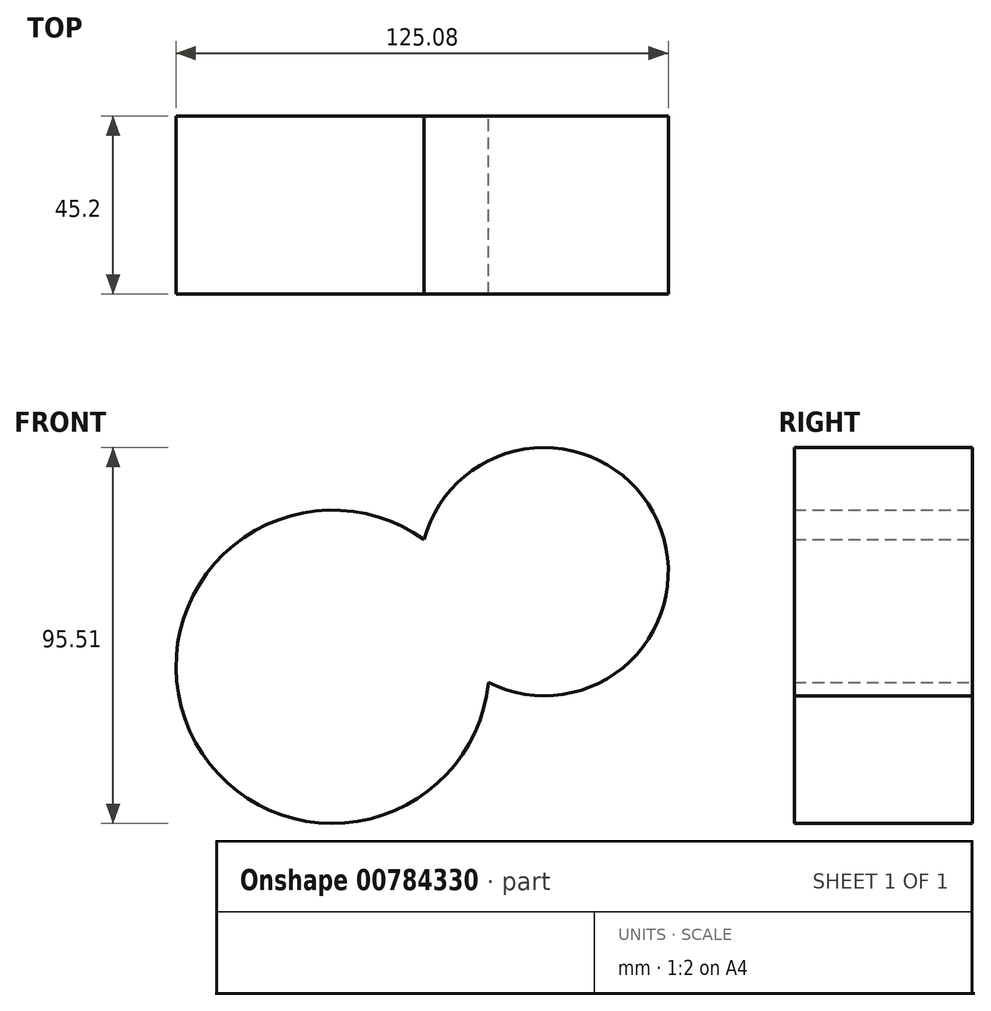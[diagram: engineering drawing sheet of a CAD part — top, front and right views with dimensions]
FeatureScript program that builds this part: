
annotation { "Feature Type Name" : "Feature", "Feature Type Description" : "" }
export const myFeature = defineFeature(function(context is Context, id is Id, definition is map)
    precondition{}
    {
        {
            var Q0;
            Q0=qCreatedBy(makeId("Front.planeOp"),FACE);
            var sketch = newSketch(context, id + "F0", { "sketchPlane" : qUnion([Q0])});
            skCircle(sketch, "E0", {"center": v(-22.89, 16.63) * mm, "radius": 39.8 * mm});
            skCircle(sketch, "E1", {"center": v(30.85, 40.8) * mm, "radius": 31.54 * mm});
            skSolve(sketch);
        }
        {
            var Q0;
            Q0 = qSketchRegion(id + "F0", true);
            extrude(context, id + "F1", {"entities" : qUnion([Q0]), "depth" : 45.2 * mm, "offsetDistance" : 25 * mm});
        }
    });
